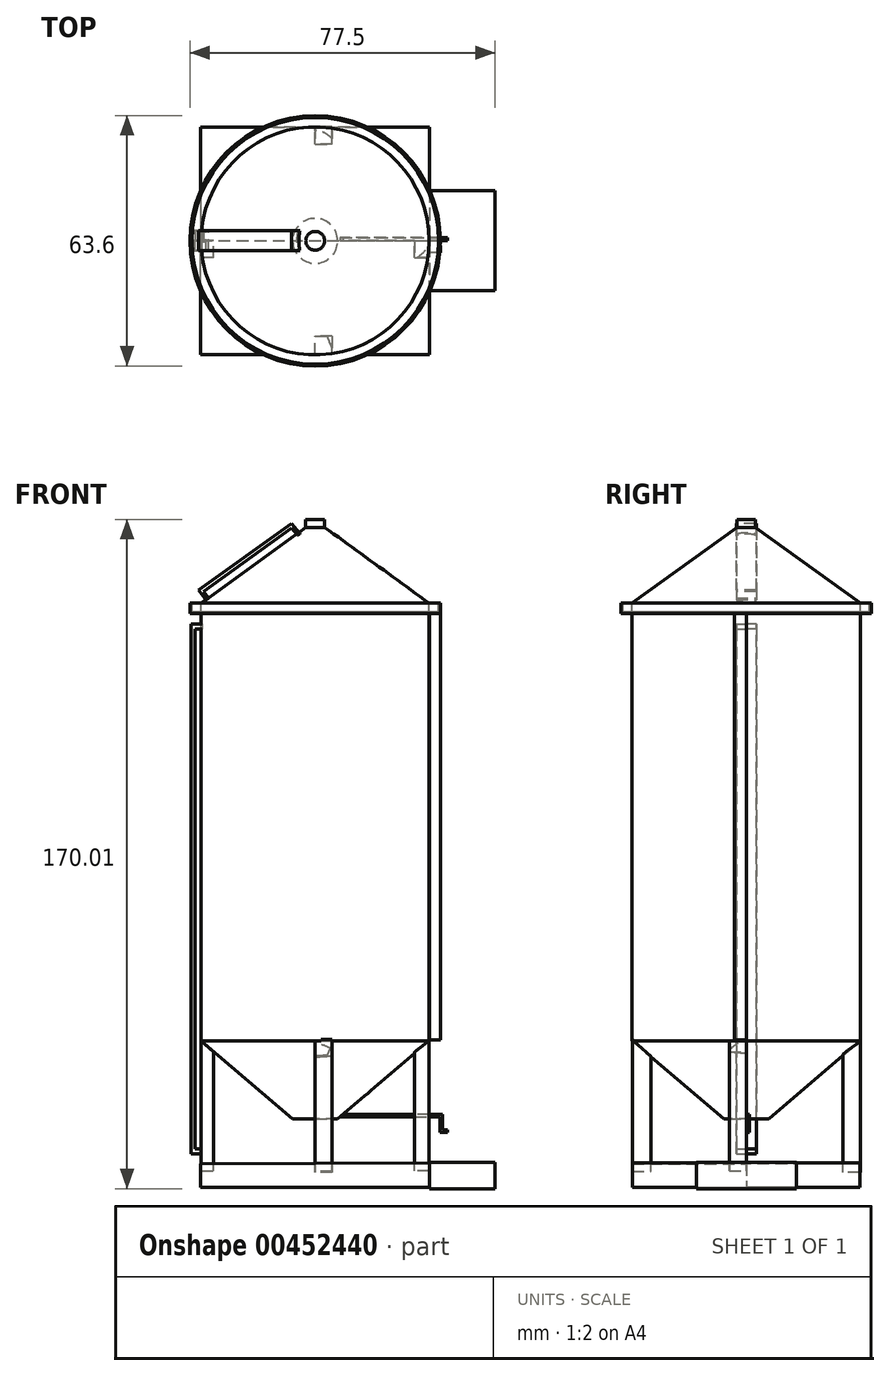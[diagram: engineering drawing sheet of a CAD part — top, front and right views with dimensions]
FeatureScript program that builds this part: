
annotation { "Feature Type Name" : "Feature", "Feature Type Description" : "" }
export const myFeature = defineFeature(function(context is Context, id is Id, definition is map)
    precondition{}
    {
        {
            var Q0;
            Q0=qCreatedBy(makeId("Front.planeOp"),FACE);
            var sketch = newSketch(context, id + "F0", { "sketchPlane" : qUnion([Q0])});
            skLineSegment(sketch, "E0", {"start": v(-28.97, 55.49) * mm, "end": v(-28.97, 53.27) * mm});
            skLineSegment(sketch, "E1", {"start": v(-28.97, 53.27) * mm, "end": v(-31.32, 53.27) * mm});
            skLineSegment(sketch, "E2", {"start": v(-31.32, 53.27) * mm, "end": v(-31.32, 55.49) * mm});
            skLineSegment(sketch, "E3", {"start": v(-31.32, 55.49) * mm, "end": v(-31.8, 55.49) * mm});
            skLineSegment(sketch, "E4", {"start": v(-31.8, 55.49) * mm, "end": v(-31.8, 52.9) * mm});
            skLineSegment(sketch, "E5", {"start": v(-31.8, 52.9) * mm, "end": v(-28.97, 52.9) * mm});
            skLineSegment(sketch, "E6", {"start": v(-28.97, 52.9) * mm, "end": v(-28.97, -55.68) * mm});
            skLineSegment(sketch, "E7", {"start": v(-28.97, 55.49) * mm, "end": v(-2.4, 74.76) * mm});
            skLineSegment(sketch, "E8", {"start": v(-2.4, 74.76) * mm, "end": v(-2.4, 76.76) * mm});
            skLineSegment(sketch, "E9", {"start": v(-2.4, 76.76) * mm, "end": v(0, 76.76) * mm});
            skLineSegment(sketch, "E10", {"start": v(0, 76.76) * mm, "end": v(0, -75.5) * mm});
            skLineSegment(sketch, "E11", {"start": v(0, -75.5) * mm, "end": v(-5.71, -75.5) * mm});
            skLineSegment(sketch, "E12", {"start": v(-5.71, -75.5) * mm, "end": v(-28.97, -55.68) * mm});
            skSolve(sketch);
        }
        {
            var Q0;
            Q0 = qSketchRegion(id + "F0", true);
            var Q1;
            Q1=makeQuery(id+"F0.imprint","IMPRINT",FACE,{"disambiguationData":[TD([[makeQuery(id+"F0.imprint","IMPRINT",EDGE,{"derivedFrom":sQuery(id+"F0.wireOp",EDGE,"E0")}),1.0]])]});
            var Q2;
            Q2=sQuery(id+"F0.wireOp",EDGE,"E10");
            revolve(context, id + "F1", {"entities" : qUnion([Q0, Q1]), "axis" : qUnion([Q2]), "revolveType" : RevolveType.FULL});
        }
        {
            var Q0;
            Q0=qCreatedBy(makeId("Front.planeOp"),FACE);
            var sketch = newSketch(context, id + "F2", { "sketchPlane" : qUnion([Q0])});
            skLineSegment(sketch, "E13", {"start": v(31.78, 52.9) * mm, "end": v(31.78, -55.5) * mm});
            skLineSegment(sketch, "E14", {"start": v(31.78, -55.5) * mm, "end": v(29, -55.5) * mm});
            skLineSegment(sketch, "E15", {"start": v(29, -55.5) * mm, "end": v(29, 52.93) * mm});
            skLineSegment(sketch, "E16", {"start": v(29, 52.93) * mm, "end": v(31.78, 52.9) * mm});
            skSolve(sketch);
        }
        {
            var Q0;
            Q0=makeQuery(id+"F2.imprint","IMPRINT",FACE,{"disambiguationData":[TD([[makeQuery(id+"F2.imprint","IMPRINT",EDGE,{"derivedFrom":sQuery(id+"F2.wireOp",EDGE,"E13")}),-1.0]])]});
            extrude(context, id + "F3", {"entities" : qUnion([Q0]), "operationType" : NewBodyOperationType.ADD, "depth" : 3.05 * mm});
        }
        {
            var Q0;
            Q0=qCreatedBy(makeId("Front.planeOp"),FACE);
            var sketch = newSketch(context, id + "F4", { "sketchPlane" : qUnion([Q0])});
            skLineSegment(sketch, "E17", {"start": v(-29, -55.7) * mm, "end": v(-29, -88.78) * mm});
            skLineSegment(sketch, "E18", {"start": v(-29, -88.78) * mm, "end": v(-25.82, -88.78) * mm});
            skLineSegment(sketch, "E19", {"start": v(-25.82, -88.78) * mm, "end": v(-25.82, -58.5) * mm});
            skLineSegment(sketch, "E20", {"start": v(-25.82, -58.5) * mm, "end": v(-29, -55.7) * mm});
            skLineSegment(sketch, "E21", {"start": v(28.96, -55.7) * mm, "end": v(28.96, -88.78) * mm});
            skLineSegment(sketch, "E22", {"start": v(28.96, -88.78) * mm, "end": v(25.25, -88.78) * mm});
            skLineSegment(sketch, "E23", {"start": v(25.25, -88.78) * mm, "end": v(25.25, -58.5) * mm});
            skLineSegment(sketch, "E24", {"start": v(25.25, -58.5) * mm, "end": v(28.96, -55.7) * mm});
            skSolve(sketch);
        }
        {
            var Q0;
            Q0=makeQuery(id+"F4.imprint","IMPRINT",FACE,{"disambiguationData":[TD([[makeQuery(id+"F4.imprint","IMPRINT",EDGE,{"derivedFrom":sQuery(id+"F4.wireOp",EDGE,"E21")}),-1.0]])]});
            var Q1;
            Q1=makeQuery(id+"F4.imprint","IMPRINT",FACE,{"disambiguationData":[TD([[makeQuery(id+"F4.imprint","IMPRINT",EDGE,{"derivedFrom":sQuery(id+"F4.wireOp",EDGE,"E17")}),1.0]])]});
            extrude(context, id + "F5", {"entities" : qUnion([Q0, Q1]), "operationType" : NewBodyOperationType.ADD, "depth" : 4.32 * mm});
        }
        {
            var Q0;
            Q0=qCreatedBy(makeId("Right.planeOp"),FACE);
            var sketch = newSketch(context, id + "F6", { "sketchPlane" : qUnion([Q0])});
            skLineSegment(sketch, "E25", {"start": v(-28.93, -55.38) * mm, "end": v(-28.93, -88.83) * mm});
            skLineSegment(sketch, "E26", {"start": v(28.96, -55.83) * mm, "end": v(28.96, -89.08) * mm});
            skLineSegment(sketch, "E27", {"start": v(28.96, -89.08) * mm, "end": v(24.6, -89.08) * mm});
            skLineSegment(sketch, "E28", {"start": v(24.6, -89.08) * mm, "end": v(24.6, -58.9) * mm});
            skLineSegment(sketch, "E29", {"start": v(24.6, -58.9) * mm, "end": v(28.96, -55.83) * mm});
            skLineSegment(sketch, "E30", {"start": v(-28.93, -88.83) * mm, "end": v(-24.9, -88.83) * mm});
            skLineSegment(sketch, "E31", {"start": v(-24.9, -88.83) * mm, "end": v(-24.21, -88.83) * mm});
            skLineSegment(sketch, "E32", {"start": v(-24.21, -88.83) * mm, "end": v(-24.21, -59.58) * mm});
            skLineSegment(sketch, "E33", {"start": v(-24.21, -59.58) * mm, "end": v(-28.93, -55.38) * mm});
            skSolve(sketch);
        }
        {
            var Q0;
            Q0=makeQuery(id+"F6.imprint","IMPRINT",FACE,{"disambiguationData":[TD([[makeQuery(id+"F6.imprint","IMPRINT",EDGE,{"derivedFrom":sQuery(id+"F6.wireOp",EDGE,"E25")}),1.0]])]});
            var Q1;
            Q1=makeQuery(id+"F6.imprint","IMPRINT",FACE,{"disambiguationData":[TD([[makeQuery(id+"F6.imprint","IMPRINT",EDGE,{"derivedFrom":sQuery(id+"F6.wireOp",EDGE,"E26")}),-1.0]])]});
            extrude(context, id + "F7", {"entities" : qUnion([Q0, Q1]), "operationType" : NewBodyOperationType.ADD, "depth" : 4.32 * mm});
        }
        {
            var Q0;
            Q0=qCreatedBy(makeId("Front.planeOp"),FACE);
            var sketch = newSketch(context, id + "F8", { "sketchPlane" : qUnion([Q0])});
            skLineSegment(sketch, "E34", {"start": v(6.68, -75.03) * mm, "end": v(31.69, -75.03) * mm});
            skLineSegment(sketch, "E35", {"start": v(31.69, -75.03) * mm, "end": v(31.69, -79) * mm});
            skLineSegment(sketch, "E36", {"start": v(31.69, -79) * mm, "end": v(33.62, -79) * mm});
            skLineSegment(sketch, "E37", {"start": v(33.62, -79) * mm, "end": v(33.62, -78.36) * mm});
            skLineSegment(sketch, "E38", {"start": v(33.62, -78.36) * mm, "end": v(32.4, -78.36) * mm});
            skLineSegment(sketch, "E39", {"start": v(32.4, -78.36) * mm, "end": v(32.4, -74.4) * mm});
            skLineSegment(sketch, "E40", {"start": v(32.4, -74.4) * mm, "end": v(7.11, -74.4) * mm});
            skLineSegment(sketch, "E41", {"start": v(7.11, -74.4) * mm, "end": v(6.3, -75.03) * mm});
            skLineSegment(sketch, "E42", {"start": v(6.3, -75.03) * mm, "end": v(6.68, -75.03) * mm});
            skSolve(sketch);
        }
        {
            var Q0;
            Q0=makeQuery(id+"F8.imprint","IMPRINT",FACE,{"disambiguationData":[TD([[makeQuery(id+"F8.imprint","IMPRINT",EDGE,{"derivedFrom":sQuery(id+"F8.wireOp",EDGE,"E34")}),1.0]])]});
            extrude(context, id + "F9", {"entities" : qUnion([Q0]), "operationType" : NewBodyOperationType.ADD, "oppositeDirection" : true, "depth" : 0.76 * mm});
        }
        {
            var Q0;
            Q0=qCreatedBy(makeId("Front.planeOp"),FACE);
            var sketch = newSketch(context, id + "F10", { "sketchPlane" : qUnion([Q0])});
            skLineSegment(sketch, "E43", {"start": v(-29.18, -87) * mm, "end": v(-29.18, -92.93) * mm});
            skLineSegment(sketch, "E44", {"start": v(28.98, -86.73) * mm, "end": v(28.98, -92.93) * mm});
            skLineSegment(sketch, "E45", {"start": v(-29.18, -92.93) * mm, "end": v(28.98, -92.93) * mm});
            skLineSegment(sketch, "E46", {"start": v(28.98, -86.73) * mm, "end": v(-29.18, -87) * mm});
            skSolve(sketch);
        }
        {
            var Q0;
            Q0=makeQuery(id+"F10.imprint","IMPRINT",FACE,{"disambiguationData":[TD([[makeQuery(id+"F10.imprint","IMPRINT",EDGE,{"derivedFrom":sQuery(id+"F10.wireOp",EDGE,"E43")}),1.0]])]});
            extrude(context, id + "F11", {"entities" : qUnion([Q0]), "oppositeDirection" : true, "depth" : 28.83 * mm});
        }
        {
            var Q0;
            Q0=makeQuery(id+"F11.opExtrude","CAP_FACE",FACE,{"disambiguationData":[OSD([sQuery(id+"F10.wireOp",EDGE,"E43"),sQuery(id+"F10.wireOp",EDGE,"E44"),sQuery(id+"F10.wireOp",EDGE,"E45"),sQuery(id+"F10.wireOp",EDGE,"E46")])],"isStart":true});
            extrude(context, id + "F12", {"entities" : qUnion([Q0]), "depth" : 28.96 * mm});
        }
        {
            var Q0;
            Q0=qCreatedBy(makeId("Front.planeOp"),FACE);
            var sketch = newSketch(context, id + "F13", { "sketchPlane" : qUnion([Q0])});
            skLineSegment(sketch, "E47", {"start": v(29, -86.6) * mm, "end": v(45.7, -86.6) * mm});
            skLineSegment(sketch, "E48", {"start": v(29, -86.6) * mm, "end": v(29, -93.25) * mm});
            skLineSegment(sketch, "E49", {"start": v(29, -93.25) * mm, "end": v(45.7, -93.25) * mm});
            skLineSegment(sketch, "E50", {"start": v(45.7, -93.25) * mm, "end": v(45.7, -86.6) * mm});
            skSolve(sketch);
        }
        {
            var Q0;
            Q0=makeQuery(id+"F13.imprint","IMPRINT",FACE,{"disambiguationData":[TD([[makeQuery(id+"F13.imprint","IMPRINT",EDGE,{"derivedFrom":sQuery(id+"F13.wireOp",EDGE,"E47")}),-1.0]])]});
            extrude(context, id + "F14", {"entities" : qUnion([Q0]), "oppositeDirection" : true, "depth" : 12.7 * mm});
        }
        {
            var Q0;
            Q0=makeQuery(id+"F14.opExtrude","CAP_FACE",FACE,{"disambiguationData":[OSD([sQuery(id+"F13.wireOp",EDGE,"E47"),sQuery(id+"F13.wireOp",EDGE,"E48"),sQuery(id+"F13.wireOp",EDGE,"E49"),sQuery(id+"F13.wireOp",EDGE,"E50")])],"isStart":true});
            extrude(context, id + "F15", {"entities" : qUnion([Q0]), "operationType" : NewBodyOperationType.ADD, "depth" : 12.7 * mm});
        }
        {
            var Q0;
            Q0=qCreatedBy(makeId("Front.planeOp"),FACE);
            var sketch = newSketch(context, id + "F16", { "sketchPlane" : qUnion([Q0])});
            skLineSegment(sketch, "E51.bottom", {"start": v(-2.28, 52.18) * mm, "end": v(1.74, 52.18) * mm});
            skLineSegment(sketch, "E51.top", {"start": v(-2.28, -53.94) * mm, "end": v(1.74, -53.94) * mm});
            skLineSegment(sketch, "E51.left", {"start": v(-2.28, 52.18) * mm, "end": v(-2.28, -53.94) * mm});
            skLineSegment(sketch, "E51.right", {"start": v(1.74, 52.18) * mm, "end": v(1.74, -53.94) * mm});
            skSolve(sketch);
        }
        {
            var Q0;
            Q0=sQuery(id+"F16.wireOp",EDGE,"E51.left");
            var Q1;
            Q1=sQuery(id+"F16.wireOp",EDGE,"E51.right");
            var Q2;
            Q2=sQuery(id+"F16.wireOp",EDGE,"E51.bottom");
            var Q3;
            Q3=sQuery(id+"F16.wireOp",EDGE,"E51.top");
            extrude(context, id + "F17", {"bodyType" : ToolBodyType.SURFACE, "surfaceEntities" : qUnion([Q0, Q1, Q2, Q3]), "oppositeDirection" : true, "depth" : 29.08 * mm});
        }
        {
            var Q0;
            Q0=qCreatedBy(makeId("Front.planeOp"),FACE);
            var sketch = newSketch(context, id + "F18", { "sketchPlane" : qUnion([Q0])});
            skLineSegment(sketch, "E52", {"start": v(-28.96, -84.4) * mm, "end": v(-31.52, -84.4) * mm});
            skLineSegment(sketch, "E53", {"start": v(-31.52, -84.4) * mm, "end": v(-31.52, 50.15) * mm});
            skLineSegment(sketch, "E54", {"start": v(-31.52, 50.15) * mm, "end": v(-28.78, 50.15) * mm});
            skLineSegment(sketch, "E55", {"start": v(-28.78, 50.15) * mm, "end": v(-28.78, 48.91) * mm});
            skLineSegment(sketch, "E56", {"start": v(-28.78, 48.91) * mm, "end": v(-30.54, 48.91) * mm});
            skLineSegment(sketch, "E57", {"start": v(-30.54, 48.91) * mm, "end": v(-30.54, -83.15) * mm});
            skLineSegment(sketch, "E58", {"start": v(-30.54, -83.15) * mm, "end": v(-28.96, -83.15) * mm});
            skLineSegment(sketch, "E59", {"start": v(-28.96, -83.15) * mm, "end": v(-28.96, -84.4) * mm});
            skSolve(sketch);
        }
        {
            var Q0;
            Q0 = qSketchRegion(id + "F18", true);
            extrude(context, id + "F19", {"entities" : qUnion([Q0]), "depth" : 2.54 * mm});
        }
        {
            var Q0;
            Q0=qCreatedBy(makeId("Front.planeOp"),FACE);
            var sketch = newSketch(context, id + "F20", { "sketchPlane" : qUnion([Q0])});
            skLineSegment(sketch, "E60", {"start": v(-29.7, 58.79) * mm, "end": v(-6.05, 75.8) * mm});
            skLineSegment(sketch, "E61", {"start": v(-6, 74.59) * mm, "end": v(-28.33, 58.53) * mm});
            skLineSegment(sketch, "E62", {"start": v(-28.33, 58.53) * mm, "end": v(-26.66, 56.2) * mm});
            skLineSegment(sketch, "E63", {"start": v(-29.7, 58.79) * mm, "end": v(-27.2, 55.7) * mm});
            skLineSegment(sketch, "E64", {"start": v(-27.2, 55.7) * mm, "end": v(-26.66, 56.2) * mm});
            skLineSegment(sketch, "E65", {"start": v(-6.05, 75.8) * mm, "end": v(-3.48, 72.65) * mm});
            skLineSegment(sketch, "E66", {"start": v(-3.48, 72.65) * mm, "end": v(-4, 72.24) * mm});
            skLineSegment(sketch, "E67", {"start": v(-4, 72.24) * mm, "end": v(-6, 74.59) * mm});
            skSolve(sketch);
        }
        {
            var Q0;
            Q0=makeQuery(id+"F20.imprint","IMPRINT",FACE,{"disambiguationData":[TD([[makeQuery(id+"F20.imprint","IMPRINT",EDGE,{"derivedFrom":sQuery(id+"F20.wireOp",EDGE,"E60")}),-1.0]])]});
            extrude(context, id + "F21", {"entities" : qUnion([Q0]), "operationType" : NewBodyOperationType.ADD, "oppositeDirection" : true, "depth" : 2.54 * mm});
        }
        {
            var Q0;
            Q0=makeQuery(id+"F21.opExtrude","CAP_FACE",FACE,{"disambiguationData":[OSD([sQuery(id+"F20.wireOp",EDGE,"E60"),sQuery(id+"F20.wireOp",EDGE,"E61"),sQuery(id+"F20.wireOp",EDGE,"E62"),sQuery(id+"F20.wireOp",EDGE,"E63"),sQuery(id+"F20.wireOp",EDGE,"E64"),sQuery(id+"F20.wireOp",EDGE,"E65"),sQuery(id+"F20.wireOp",EDGE,"E66"),sQuery(id+"F20.wireOp",EDGE,"E67")])],"isStart":false});
            extrude(context, id + "F22", {"entities" : qUnion([Q0]), "operationType" : NewBodyOperationType.ADD, "oppositeDirection" : true, "depth" : 5.08 * mm});
        }
        {
            var Q0;
            Q0=makeQuery(id+"F19.opExtrude","CAP_FACE",FACE,{"disambiguationData":[OSD([sQuery(id+"F18.wireOp",EDGE,"E52"),sQuery(id+"F18.wireOp",EDGE,"E53"),sQuery(id+"F18.wireOp",EDGE,"E54"),sQuery(id+"F18.wireOp",EDGE,"E55"),sQuery(id+"F18.wireOp",EDGE,"E56"),sQuery(id+"F18.wireOp",EDGE,"E57"),sQuery(id+"F18.wireOp",EDGE,"E58"),sQuery(id+"F18.wireOp",EDGE,"E59")])],"isStart":true});
            extrude(context, id + "F23", {"entities" : qUnion([Q0]), "depth" : 2.54 * mm});
        }
    });
